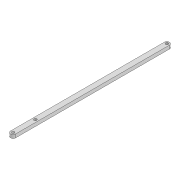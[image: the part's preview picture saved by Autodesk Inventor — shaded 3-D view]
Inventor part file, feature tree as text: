
AUTODESK INVENTOR PART (.ipt)
format: ipt  version: 2022 (Build 260153000, 153)  size: 92,672 bytes
history: native  units: mm
features: extrude x1, sketch x1
ambient origin geometry x8: Origin, YZ Plane, XZ Plane, XY Plane, X Axis, Y Axis, Z Axis, Center Point
bodies: Solid1 (feature_tree)
feature tree (2):
  extrude  "Extrusion1"  Depth=26.043mm
  sketch  "Sketch1"  dims[d0=3.2mm d1=3.2mm d2=6.0mm d3=180.271mm d6=4.0mm d7=0.0mm d14=3.2mm d15=26.043mm]
